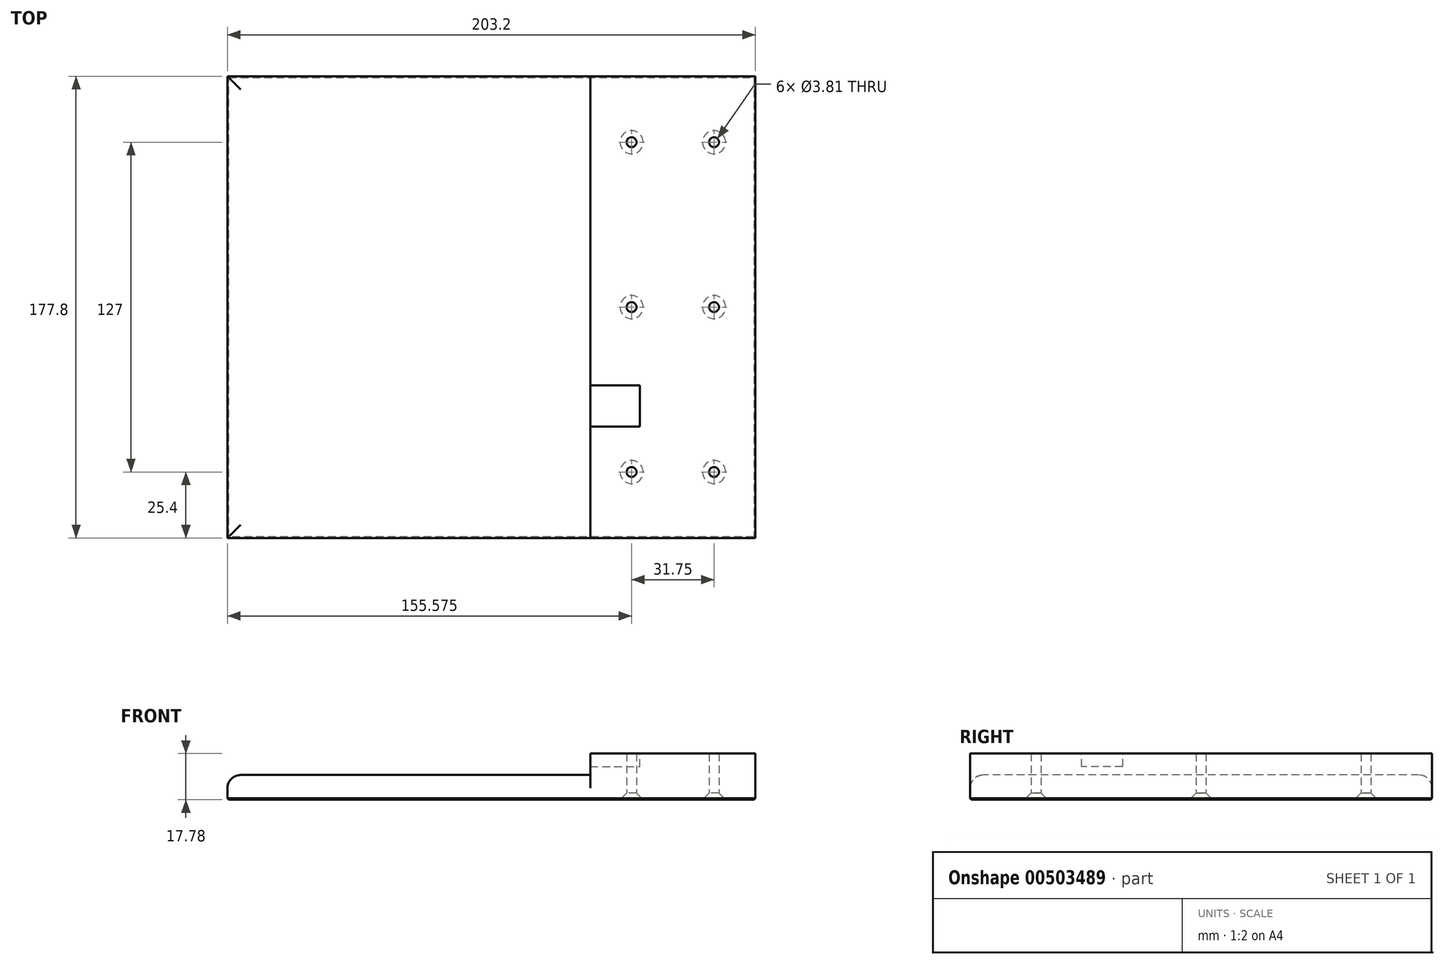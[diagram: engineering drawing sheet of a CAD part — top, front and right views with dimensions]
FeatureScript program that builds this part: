
annotation { "Feature Type Name" : "Feature", "Feature Type Description" : "" }
export const myFeature = defineFeature(function(context is Context, id is Id, definition is map)
    precondition{}
    {
        {
            var Q0;
            Q0=qCreatedBy(makeId("Top.planeOp"),FACE);
            var sketch = newSketch(context, id + "F0", { "sketchPlane" : qUnion([Q0])});
            skLineSegment(sketch, "E0.bottom", {"start": v(101.6, -88.9) * mm, "end": v(-101.6, -88.9) * mm});
            skLineSegment(sketch, "E0.top", {"start": v(101.6, 88.9) * mm, "end": v(-101.6, 88.9) * mm});
            skLineSegment(sketch, "E0.left", {"start": v(101.6, -88.9) * mm, "end": v(101.6, 88.9) * mm});
            skLineSegment(sketch, "E0.right", {"start": v(-101.6, -88.9) * mm, "end": v(-101.6, 88.9) * mm});
            skPoint(sketch, "E0.middle", {"position": v(0, 0) * mm});
            skLineSegment(sketch, "E1", {"start": v(38.1, 88.9) * mm, "end": v(38.1, -88.9) * mm});
            skCircle(sketch, "E2", {"center": v(53.97, 63.5) * mm, "radius": 1.9 * mm});
            skCircle(sketch, "E3", {"center": v(85.72, 63.5) * mm, "radius": 1.9 * mm});
            skCircle(sketch, "E4", {"center": v(53.97, 0) * mm, "radius": 1.9 * mm});
            skCircle(sketch, "E5", {"center": v(85.72, 0) * mm, "radius": 1.9 * mm});
            skCircle(sketch, "E6", {"center": v(53.98, -63.5) * mm, "radius": 1.9 * mm});
            skCircle(sketch, "E7", {"center": v(85.72, -63.5) * mm, "radius": 1.9 * mm});
            skSolve(sketch);
        }
        {
            var Q0;
            {var subQ2=sQuery(id+"F0.wireOp",EDGE,"E0.right");Q0=makeQuery(id+"F0.imprint","IMPRINT",FACE,{"disambiguationData":[TD([[makeQuery(id+"F0.imprint","IMPRINT",EDGE,{"derivedFrom":subQ2}),-1.0]])]});}
            extrude(context, id + "F1", {"entities" : qUnion([Q0]), "depth" : 9.52 * mm, "offsetDistance" : 25.4 * mm});
        }
        {
            var Q0;
            {var subQ0=sQuery(id+"F0.wireOp",EDGE,"E0.left");Q0=makeQuery(id+"F0.imprint","IMPRINT",FACE,{"disambiguationData":[TD([[makeQuery(id+"F0.imprint","IMPRINT",EDGE,{"derivedFrom":subQ0}),1.0]])]});}
            extrude(context, id + "F2", {"entities" : qUnion([Q0]), "operationType" : NewBodyOperationType.ADD, "depth" : 17.78 * mm, "offsetDistance" : 25.4 * mm});
        }
        {
            var Q0;
            Q0=makeQuery(id+"F2.opExtrude","CAP_EDGE",EDGE,{"disambiguationData":[OSD([sQuery(id+"F0.wireOp",EDGE,"E6")])],"isStart":true});
            var Q1;
            Q1=makeQuery(id+"F2.opExtrude","CAP_EDGE",EDGE,{"disambiguationData":[OSD([sQuery(id+"F0.wireOp",EDGE,"E7")])],"isStart":true});
            var Q2;
            Q2=makeQuery(id+"F2.opExtrude","CAP_EDGE",EDGE,{"disambiguationData":[OSD([sQuery(id+"F0.wireOp",EDGE,"E4")])],"isStart":true});
            var Q3;
            Q3=makeQuery(id+"F2.opExtrude","CAP_EDGE",EDGE,{"disambiguationData":[OSD([sQuery(id+"F0.wireOp",EDGE,"E5")])],"isStart":true});
            var Q4;
            Q4=makeQuery(id+"F2.opExtrude","CAP_EDGE",EDGE,{"disambiguationData":[OSD([sQuery(id+"F0.wireOp",EDGE,"E2")])],"isStart":true});
            var Q5;
            Q5=makeQuery(id+"F2.opExtrude","CAP_EDGE",EDGE,{"disambiguationData":[OSD([sQuery(id+"F0.wireOp",EDGE,"E3")])],"isStart":true});
            chamfer(context, id + "F3", {"entities" : qUnion([Q0, Q1, Q2, Q3, Q4, Q5]), "width" : 2.54 * mm, "tangentPropagation" : true});
        }
        {
            var Q0;
            {var subQ0=sQuery(id+"F0.wireOp",EDGE,"E0.bottom");Q0=makeQuery(id+"F2.boolean.opBoolean","MERGE",EDGE,{"derivedFrom":[makeQuery(id+"F1.opExtrude","CAP_EDGE",EDGE,{"disambiguationData":[OSD([subQ0])],"isStart":true}),makeQuery(id+"F2.opExtrude","CAP_EDGE",EDGE,{"disambiguationData":[OSD([subQ0])],"isStart":true})]});}
            var Q1;
            Q1=makeQuery(id+"F2.opExtrude","CAP_EDGE",EDGE,{"disambiguationData":[OSD([sQuery(id+"F0.wireOp",EDGE,"E0.left")])],"isStart":true});
            var Q2;
            {var subQ0=sQuery(id+"F0.wireOp",EDGE,"E0.top");Q2=makeQuery(id+"F2.boolean.opBoolean","MERGE",EDGE,{"derivedFrom":[makeQuery(id+"F1.opExtrude","CAP_EDGE",EDGE,{"disambiguationData":[OSD([subQ0])],"isStart":true}),makeQuery(id+"F2.opExtrude","CAP_EDGE",EDGE,{"disambiguationData":[OSD([subQ0])],"isStart":true})]});}
            var Q3;
            Q3=makeQuery(id+"F1.opExtrude","CAP_EDGE",EDGE,{"disambiguationData":[OSD([sQuery(id+"F0.wireOp",EDGE,"E0.right")])],"isStart":true});
            chamfer(context, id + "F4", {"entities" : qUnion([Q0, Q1, Q2, Q3]), "width" : 0.5 * mm, "tangentPropagation" : true});
        }
        {
            var Q0;
            Q0=makeQuery(id+"F1.opExtrude","CAP_EDGE",EDGE,{"disambiguationData":[OSD([sQuery(id+"F0.wireOp",EDGE,"E0.bottom")])],"isStart":false});
            var Q1;
            Q1=makeQuery(id+"F1.opExtrude","CAP_EDGE",EDGE,{"disambiguationData":[OSD([sQuery(id+"F0.wireOp",EDGE,"E0.right")])],"isStart":false});
            var Q2;
            Q2=makeQuery(id+"F1.opExtrude","CAP_EDGE",EDGE,{"disambiguationData":[OSD([sQuery(id+"F0.wireOp",EDGE,"E0.top")])],"isStart":false});
            fillet(context, id + "F5", {"entities" : qUnion([Q0, Q1, Q2]), "tangentPropagation" : true, "radius" : 5.08 * mm, "defaultsChanged" : false, "vertexSettings" : [], "allowEdgeOverflow" : false});
        }
        {
            var Q0;
            Q0=makeQuery(id+"F2.opExtrude","CAP_FACE",FACE,{"disambiguationData":[OSD([sQuery(id+"F0.wireOp",EDGE,"E0.bottom"),sQuery(id+"F0.wireOp",EDGE,"E0.top"),sQuery(id+"F0.wireOp",EDGE,"E0.left"),sQuery(id+"F0.wireOp",EDGE,"E1"),sQuery(id+"F0.wireOp",EDGE,"E2"),sQuery(id+"F0.wireOp",EDGE,"E3"),sQuery(id+"F0.wireOp",EDGE,"E4"),sQuery(id+"F0.wireOp",EDGE,"E5"),sQuery(id+"F0.wireOp",EDGE,"E6"),sQuery(id+"F0.wireOp",EDGE,"E7")])],"isStart":false});
            var sketch = newSketch(context, id + "F6", { "sketchPlane" : qUnion([Q0])});
            skLineSegment(sketch, "E8", {"start": v(38.1, -46.04) * mm, "end": v(57.15, -46.04) * mm});
            skLineSegment(sketch, "E9", {"start": v(57.15, -46.04) * mm, "end": v(57.15, -30.16) * mm});
            skLineSegment(sketch, "E10", {"start": v(57.15, -30.16) * mm, "end": v(38.1, -30.16) * mm});
            skLineSegment(sketch, "E11", {"start": v(57.15, -38.1) * mm, "end": v(101.6, -38.1) * mm, "construction": true});
            skSolve(sketch);
        }
        {
            var Q0;
            {var subQ0=sQuery(id+"F6.wireOp",EDGE,"E8");Q0=makeQuery(id+"F6.imprint","IMPRINT",FACE,{"disambiguationData":[TD([[makeQuery(id+"F6.imprint","IMPRINT",EDGE,{"derivedFrom":subQ0}),1.0]])]});}
            extrude(context, id + "F7", {"entities" : qUnion([Q0]), "operationType" : NewBodyOperationType.REMOVE, "oppositeDirection" : true, "depth" : 5.08 * mm, "offsetDistance" : 25.4 * mm});
        }
    });
